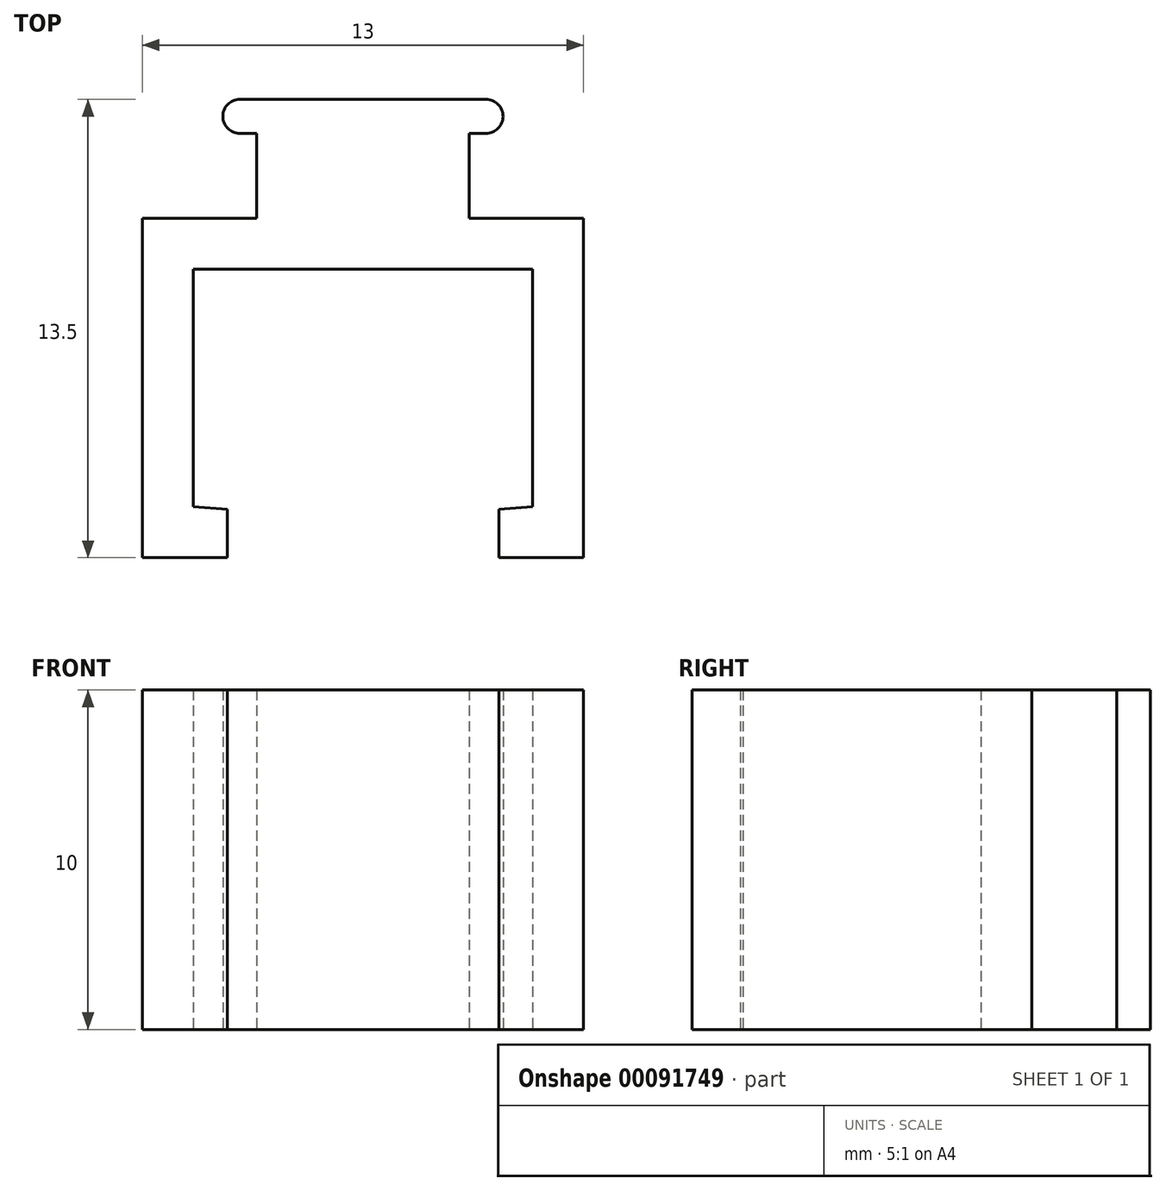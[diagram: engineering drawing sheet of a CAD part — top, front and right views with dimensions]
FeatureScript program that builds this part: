
annotation { "Feature Type Name" : "Feature", "Feature Type Description" : "" }
export const myFeature = defineFeature(function(context is Context, id is Id, definition is map)
    precondition{}
    {
        {
            var Q0;
            Q0=qCreatedBy(makeId("Top.planeOp"),FACE);
            var sketch = newSketch(context, id + "F0", { "sketchPlane" : qUnion([Q0])});
            skLineSegment(sketch, "E0.bottom", {"start": v(5, 3.5) * mm, "end": v(-5, 3.5) * mm, "construction": true});
            skLineSegment(sketch, "E0.top", {"start": v(5, -3.5) * mm, "end": v(-5, -3.5) * mm, "construction": true});
            skLineSegment(sketch, "E0.left", {"start": v(5, 3.5) * mm, "end": v(5, -3.5) * mm, "construction": true});
            skLineSegment(sketch, "E0.right", {"start": v(-5, 3.5) * mm, "end": v(-5, -3.5) * mm, "construction": true});
            skPoint(sketch, "E0.middle", {"position": v(0, 0) * mm});
            skLineSegment(sketch, "E1.bottom", {"start": v(3.12, 3.5) * mm, "end": v(-3.12, 3.5) * mm, "construction": true});
            skLineSegment(sketch, "E1.top", {"start": v(3.12, 9.5) * mm, "end": v(-3.13, 9.5) * mm, "construction": true});
            skLineSegment(sketch, "E1.left", {"start": v(3.12, 3.5) * mm, "end": v(3.12, 9.5) * mm, "construction": true});
            skLineSegment(sketch, "E1.right", {"start": v(-3.12, 3.5) * mm, "end": v(-3.13, 9.5) * mm, "construction": true});
            skPoint(sketch, "E1.middle", {"position": v(0, 6.5) * mm});
            skLineSegment(sketch, "E2.bottom", {"start": v(6.5, -5) * mm, "end": v(-6.5, -5) * mm, "construction": true});
            skLineSegment(sketch, "E2.top", {"start": v(6.5, 5) * mm, "end": v(-6.5, 5) * mm, "construction": true});
            skLineSegment(sketch, "E2.left", {"start": v(6.5, -5) * mm, "end": v(6.5, 5) * mm, "construction": true});
            skLineSegment(sketch, "E2.right", {"start": v(-6.5, -5) * mm, "end": v(-6.5, 5) * mm, "construction": true});
            skLineSegment(sketch, "E3.bottom", {"start": v(4, -5) * mm, "end": v(-4, -5) * mm, "construction": true});
            skLineSegment(sketch, "E3.top", {"start": v(4, -3.58) * mm, "end": v(-4, -3.58) * mm, "construction": true});
            skLineSegment(sketch, "E3.left", {"start": v(4, -5) * mm, "end": v(4, -3.58) * mm, "construction": true});
            skLineSegment(sketch, "E3.right", {"start": v(-4, -5) * mm, "end": v(-4, -3.58) * mm, "construction": true});
            skPoint(sketch, "E3.middle", {"position": v(0, -4.29) * mm});
            skLineSegment(sketch, "E4", {"start": v(-4, -5) * mm, "end": v(-6.5, -5) * mm});
            skLineSegment(sketch, "E5", {"start": v(-6.5, -5) * mm, "end": v(-6.5, 5) * mm});
            skLineSegment(sketch, "E6", {"start": v(-6.5, 5) * mm, "end": v(-3.13, 5) * mm});
            skLineSegment(sketch, "E7", {"start": v(-4, -5) * mm, "end": v(-4, -3.58) * mm});
            skLineSegment(sketch, "E8", {"start": v(-4, -3.58) * mm, "end": v(-5, -3.5) * mm});
            skLineSegment(sketch, "E9", {"start": v(-5, -3.5) * mm, "end": v(-5, 3.5) * mm});
            skLineSegment(sketch, "E10", {"start": v(-5, 3.5) * mm, "end": v(5, 3.5) * mm});
            skLineSegment(sketch, "E11", {"start": v(5, 3.5) * mm, "end": v(5, -3.5) * mm});
            skLineSegment(sketch, "E12", {"start": v(5, -3.5) * mm, "end": v(4, -3.58) * mm});
            skLineSegment(sketch, "E13", {"start": v(4, -3.58) * mm, "end": v(4, -5) * mm});
            skLineSegment(sketch, "E14", {"start": v(4, -5) * mm, "end": v(6.5, -5) * mm});
            skLineSegment(sketch, "E15", {"start": v(6.5, -5) * mm, "end": v(6.5, 5) * mm});
            skLineSegment(sketch, "E16", {"start": v(6.5, 5) * mm, "end": v(3.12, 5) * mm});
            skLineSegment(sketch, "E17.bottom", {"start": v(4.13, 7.5) * mm, "end": v(-4.13, 7.5) * mm, "construction": true});
            skLineSegment(sketch, "E17.top", {"start": v(4.13, 8.5) * mm, "end": v(-4.13, 8.5) * mm, "construction": true});
            skLineSegment(sketch, "E17.left", {"start": v(4.13, 7.5) * mm, "end": v(4.13, 8.5) * mm, "construction": true});
            skLineSegment(sketch, "E17.right", {"start": v(-4.13, 7.5) * mm, "end": v(-4.13, 8.5) * mm, "construction": true});
            skPoint(sketch, "E17.middle", {"position": v(0, 8) * mm});
            skLineSegment(sketch, "E18", {"start": v(-3.13, 5) * mm, "end": v(-3.13, 7.5) * mm});
            skLineSegment(sketch, "E19", {"start": v(-3.13, 7.5) * mm, "end": v(-3.63, 7.5) * mm});
            skLineSegment(sketch, "E20", {"start": v(3.12, 5) * mm, "end": v(3.12, 7.5) * mm});
            skLineSegment(sketch, "E21", {"start": v(-4.13, 8.5) * mm, "end": v(-3.13, 7.5) * mm, "construction": true});
            skLineSegment(sketch, "E22", {"start": v(-4.13, 7.5) * mm, "end": v(-3.63, 8) * mm, "construction": true});
            skLineSegment(sketch, "E23", {"start": v(4.13, 8.5) * mm, "end": v(3.12, 7.5) * mm, "construction": true});
            skLineSegment(sketch, "E24", {"start": v(4.13, 7.5) * mm, "end": v(3.63, 8) * mm, "construction": true});
            skPoint(sketch, "E24.endSnap0", {"position": v(3.63, 8) * mm});
            skLineSegment(sketch, "E25", {"start": v(-3.63, 8.5) * mm, "end": v(3.63, 8.5) * mm});
            skArc(sketch, "E26", {"start": v(-3.63, 8.5) * mm, "mid": v(-4.13, 8) * mm, "end": v(-3.63, 7.5) * mm});
            skArc(sketch, "E27.MirrorCS", {"start": v(3.63, 8.5) * mm, "mid": v(4.13, 8) * mm, "end": v(3.63, 7.5) * mm});
            skLineSegment(sketch, "E28", {"start": v(3.63, 7.5) * mm, "end": v(3.12, 7.5) * mm});
            skSolve(sketch);
        }
        {
            var Q0;
            Q0=makeQuery(id+"F0.imprint","IMPRINT",FACE,{"disambiguationData":[TD([[makeQuery(id+"F0.imprint","IMPRINT",EDGE,{"derivedFrom":sQuery(id+"F0.wireOp",EDGE,"E4")}),-1.0]])]});
            extrude(context, id + "F1", {"entities" : qUnion([Q0]), "depth" : 10 * mm});
        }
    });
